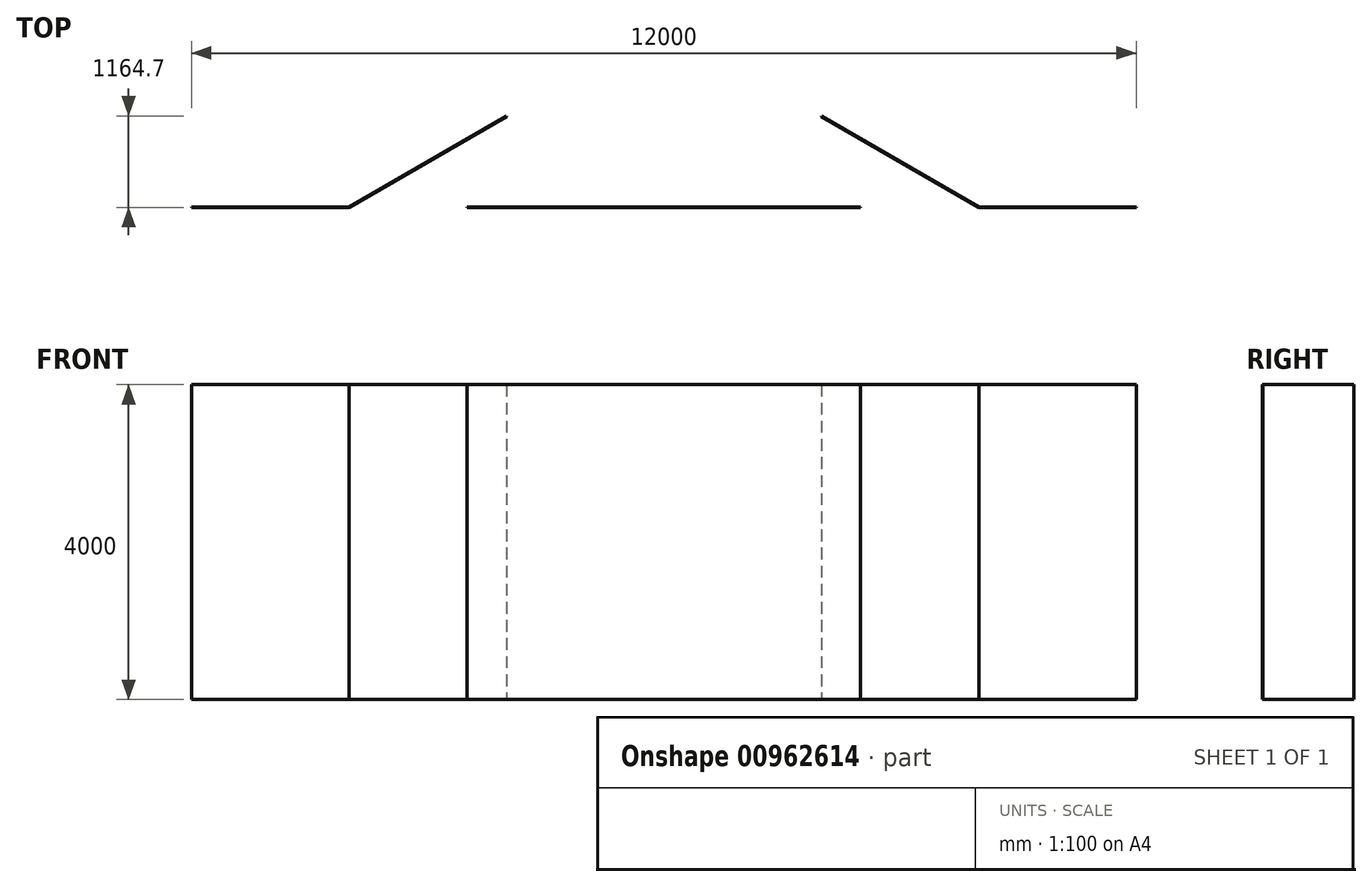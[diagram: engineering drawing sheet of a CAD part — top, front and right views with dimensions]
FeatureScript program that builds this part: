
annotation { "Feature Type Name" : "Feature", "Feature Type Description" : "" }
export const myFeature = defineFeature(function(context is Context, id is Id, definition is map)
    precondition{}
    {
        {
            var Q0;
            Q0=qCreatedBy(makeId("Top.planeOp"),FACE);
            var sketch = newSketch(context, id + "F0", { "sketchPlane" : qUnion([Q0])});
            skLineSegment(sketch, "E0", {"start": v(-2500, 0) * mm, "end": v(2500, 0) * mm});
            skLineSegment(sketch, "E1", {"start": v(2500, 0) * mm, "end": v(4000, 0) * mm, "construction": true});
            skLineSegment(sketch, "E2", {"start": v(4000, 0) * mm, "end": v(6000, 0) * mm});
            skLineSegment(sketch, "E3", {"start": v(6000, 0) * mm, "end": v(6000, 10) * mm});
            skLineSegment(sketch, "E4", {"start": v(4000, 0) * mm, "end": v(2000, 1154.7) * mm});
            skLineSegment(sketch, "E5", {"start": v(2000, 0) * mm, "end": v(2000, 1837.55) * mm, "construction": true});
            skLineSegment(sketch, "E6", {"start": v(-2500, 0) * mm, "end": v(-2500, 10) * mm});
            skLineSegment(sketch, "E7", {"start": v(-2500, 10) * mm, "end": v(2500, 10) * mm});
            skLineSegment(sketch, "E8", {"start": v(2500, 10) * mm, "end": v(2500, 0) * mm});
            skLineSegment(sketch, "E9", {"start": v(2000, 1154.7) * mm, "end": v(2000, 1164.7) * mm});
            skLineSegment(sketch, "E10", {"start": v(2000, 1164.7) * mm, "end": v(4000, 10) * mm});
            skLineSegment(sketch, "E11", {"start": v(6000, 10) * mm, "end": v(4000, 10) * mm});
            skLineSegment(sketch, "E12", {"start": v(0, -1115.83) * mm, "end": v(0, 2479.05) * mm, "construction": true});
            skLineSegment(sketch, "E13.MirrorCS", {"start": v(-6000, 0) * mm, "end": v(-6000, 10) * mm});
            skLineSegment(sketch, "E14.MirrorCS", {"start": v(-2000, 1154.7) * mm, "end": v(-2000, 1164.7) * mm});
            skLineSegment(sketch, "E15.MirrorCS", {"start": v(-4000, 0) * mm, "end": v(-6000, 0) * mm});
            skLineSegment(sketch, "E16.MirrorCS", {"start": v(-6000, 10) * mm, "end": v(-4000, 10) * mm});
            skLineSegment(sketch, "E17.MirrorCS", {"start": v(-2500, 0) * mm, "end": v(-4000, 0) * mm, "construction": true});
            skLineSegment(sketch, "E18.MirrorCS", {"start": v(-2000, 0) * mm, "end": v(-2000, 1837.55) * mm, "construction": true});
            skLineSegment(sketch, "E19.MirrorCS", {"start": v(-2000, 1164.7) * mm, "end": v(-4000, 10) * mm});
            skLineSegment(sketch, "E20.MirrorCS", {"start": v(-4000, 0) * mm, "end": v(-2000, 1154.7) * mm});
            skSolve(sketch);
        }
        {
            var Q0;
            Q0 = qSketchRegion(id + "F0", true);
            extrude(context, id + "F1", {"entities" : qUnion([Q0]), "depth" : 4000 * mm, "offsetDistance" : 25 * mm});
        }
    });
